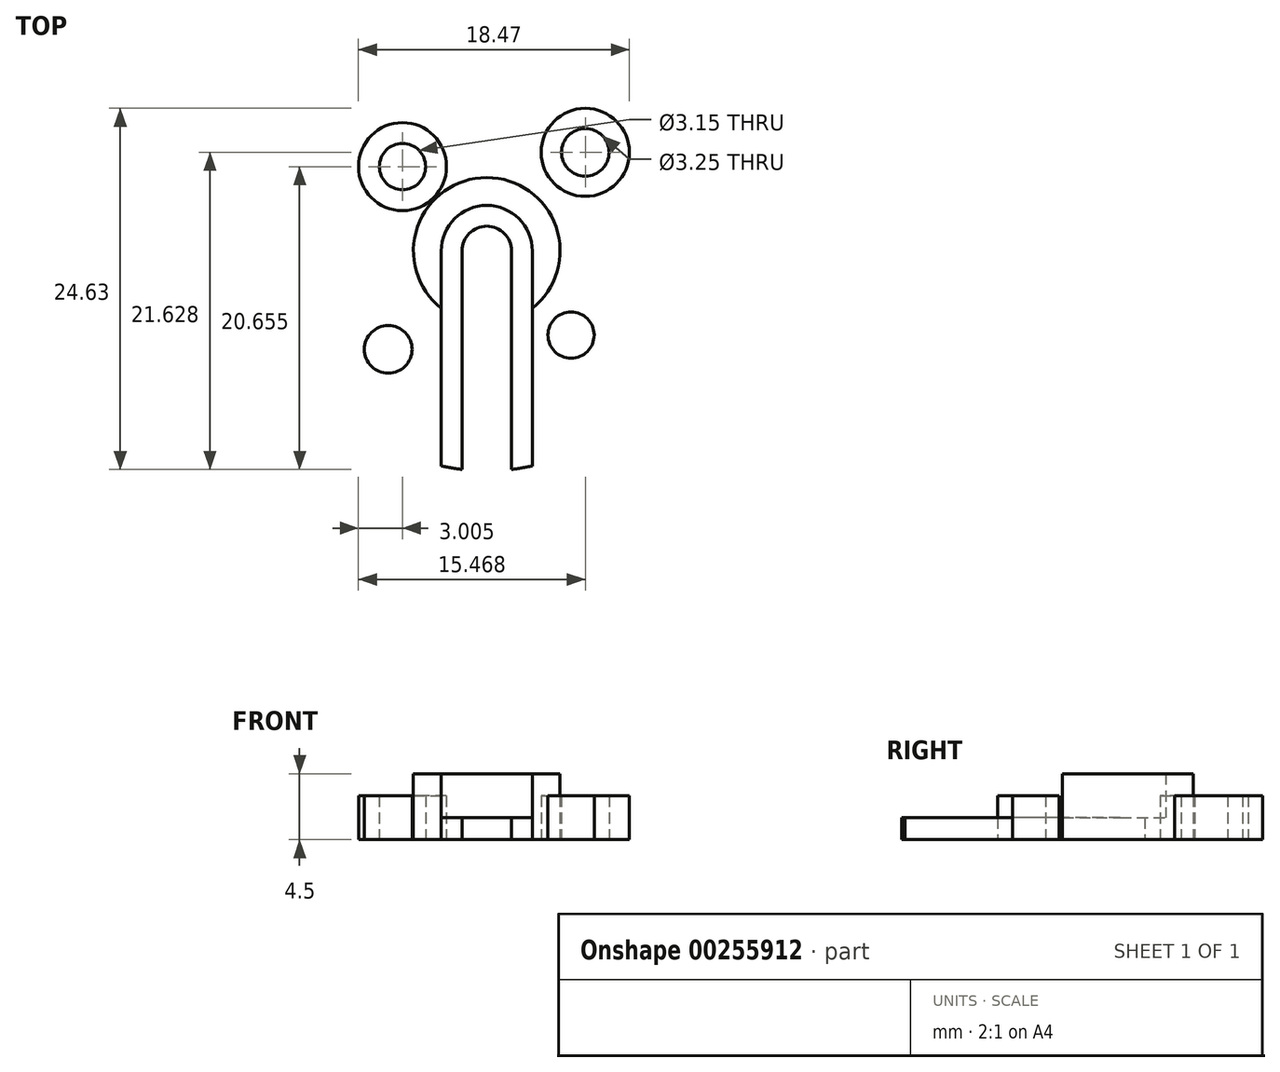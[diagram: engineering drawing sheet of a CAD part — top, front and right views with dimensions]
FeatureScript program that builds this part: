
annotation { "Feature Type Name" : "Feature", "Feature Type Description" : "" }
export const myFeature = defineFeature(function(context is Context, id is Id, definition is map)
    precondition{}
    {
        {
            var Q0;
            Q0=qCreatedBy(makeId("Top.planeOp"),FACE);
            var sketch = newSketch(context, id + "F0", { "sketchPlane" : qUnion([Q0])});
            skCircle(sketch, "E0", {"center": v(0, 0) * mm, "radius": 1.68 * mm});
            skCircle(sketch, "E1", {"center": v(0, 0) * mm, "radius": 3.1 * mm});
            skCircle(sketch, "E2", {"center": v(0, 0) * mm, "radius": 5 * mm});
            skLineSegment(sketch, "E3", {"start": v(-1.68, 0) * mm, "end": v(-1.68, -14.9) * mm});
            skLineSegment(sketch, "E4", {"start": v(-3.1, 0) * mm, "end": v(-3.1, -14.68) * mm});
            skLineSegment(sketch, "E5.MirrorCS", {"start": v(1.68, 0) * mm, "end": v(1.68, -14.9) * mm});
            skLineSegment(sketch, "E6.MirrorCS", {"start": v(3.1, 0) * mm, "end": v(3.1, -14.68) * mm});
            skCircle(sketch, "E7", {"center": v(0, 0) * mm, "radius": 9.5 * mm, "construction": true});
            skCircle(sketch, "E8", {"center": v(0, 0) * mm, "radius": 8.12 * mm, "construction": true});
            skCircle(sketch, "E9", {"center": v(-5.75, 5.75) * mm, "radius": 1.57 * mm});
            skCircle(sketch, "E10", {"center": v(6.72, 6.72) * mm, "radius": 1.63 * mm});
            skLineSegment(sketch, "E11", {"start": v(0, 0) * mm, "end": v(-5.75, 5.75) * mm, "construction": true});
            skLineSegment(sketch, "E12", {"start": v(0, 0) * mm, "end": v(6.72, 6.72) * mm, "construction": true});
            skCircle(sketch, "E13.MirrorC", {"center": v(5.75, -5.75) * mm, "radius": 1.57 * mm});
            skCircle(sketch, "E14.MirrorC", {"center": v(-6.72, -6.72) * mm, "radius": 1.63 * mm});
            skCircle(sketch, "E15", {"center": v(0, 0) * mm, "radius": 15 * mm});
            skCircle(sketch, "E16", {"center": v(-12.42, 0) * mm, "radius": 1.57 * mm});
            skCircle(sketch, "E17.MirrorC", {"center": v(12.42, 0) * mm, "radius": 1.57 * mm});
            skCircle(sketch, "E18.MirrorC", {"center": v(0, 12.42) * mm, "radius": 1.57 * mm});
            skCircle(sketch, "E19", {"center": v(-6.72, -6.72) * mm, "radius": 3 * mm});
            skCircle(sketch, "E20", {"center": v(5.75, -5.75) * mm, "radius": 3 * mm});
            skCircle(sketch, "E21.MirrorC", {"center": v(6.72, 6.72) * mm, "radius": 3 * mm});
            skCircle(sketch, "E22.MirrorC", {"center": v(-5.75, 5.75) * mm, "radius": 3 * mm});
            skSolve(sketch);
        }
        {
            var Q0;
            {var subQ0=sQuery(id+"F0.wireOp",EDGE,"E4");Q0=makeQuery(id+"F0.imprint","IMPRINT",FACE,{"disambiguationData":[TD([[makeQuery(id+"F0.imprint","IMPRINT",EDGE,{"derivedFrom":subQ0}),1.0]])]});}
            var Q1;
            {var subQ0=sQuery(id+"F0.wireOp",EDGE,"E6.MirrorCS");Q1=makeQuery(id+"F0.imprint","IMPRINT",FACE,{"disambiguationData":[TD([[makeQuery(id+"F0.imprint","IMPRINT",EDGE,{"derivedFrom":subQ0}),-1.0]])]});}
            var Q2;
            {var subQ2=sQuery(id+"F0.wireOp",EDGE,"E3");var subQ6=sQuery(id+"F0.wireOp",EDGE,"E0");var subQ9=makeQuery(id+"F0.imprint","INTERSECT",VERTEX,{"derivedFrom":[subQ6,subQ2]});Q2=makeQuery(id+"F0.imprint","IMPRINT",FACE,{"disambiguationData":[TD([[makeQuery(id+"F0.imprint","IMPRINT",EDGE,{"disambiguationData":[TD([[subQ9,1.0]])],"derivedFrom":subQ6}),-1.0]])]});}
            var Q3;
            {var subQ0=sQuery(id+"F0.wireOp",EDGE,"E19");var subQ1=sQuery(id+"F0.wireOp",EDGE,"E4");var subQ2=makeQuery(id+"F0.imprint","INTERSECT",VERTEX,{"disambiguationData":[OD(0.0)],"derivedFrom":[subQ1,subQ0]});Q3=makeQuery(id+"F0.imprint","IMPRINT",FACE,{"disambiguationData":[TD([[makeQuery(id+"F0.imprint","IMPRINT",EDGE,{"disambiguationData":[TD([[subQ2,-1.0]])],"derivedFrom":subQ1}),1.0]])]});}
            var Q4;
            {var subQ0=sQuery(id+"F0.wireOp",EDGE,"E4");var subQ1=sQuery(id+"F0.wireOp",EDGE,"E1");var subQ2=makeQuery(id+"F0.imprint","INTERSECT",VERTEX,{"derivedFrom":[subQ1,subQ0]});Q4=makeQuery(id+"F0.imprint","IMPRINT",FACE,{"disambiguationData":[TD([[makeQuery(id+"F0.imprint","IMPRINT",EDGE,{"disambiguationData":[TD([[subQ2,-1.0]])],"derivedFrom":subQ1}),-1.0]])]});}
            var Q5;
            {var subQ0=sQuery(id+"F0.wireOp",EDGE,"E4");var subQ1=sQuery(id+"F0.wireOp",EDGE,"E1");var subQ2=makeQuery(id+"F0.imprint","INTERSECT",VERTEX,{"derivedFrom":[subQ1,subQ0]});Q5=makeQuery(id+"F0.imprint","IMPRINT",FACE,{"disambiguationData":[TD([[makeQuery(id+"F0.imprint","IMPRINT",EDGE,{"disambiguationData":[TD([[subQ2,1.0]])],"derivedFrom":subQ1}),-1.0]])]});}
            var Q6;
            {var subQ0=sQuery(id+"F0.wireOp",EDGE,"E6.MirrorCS");var subQ1=sQuery(id+"F0.wireOp",EDGE,"E1");var subQ2=makeQuery(id+"F0.imprint","INTERSECT",VERTEX,{"derivedFrom":[subQ1,subQ0]});Q6=makeQuery(id+"F0.imprint","IMPRINT",FACE,{"disambiguationData":[TD([[makeQuery(id+"F0.imprint","IMPRINT",EDGE,{"disambiguationData":[TD([[subQ2,1.0]])],"derivedFrom":subQ1}),-1.0]])]});}
            var Q7;
            {var subQ0=sQuery(id+"F0.wireOp",EDGE,"E20");var subQ1=sQuery(id+"F0.wireOp",EDGE,"E6.MirrorCS");var subQ2=makeQuery(id+"F0.imprint","INTERSECT",VERTEX,{"disambiguationData":[OD(0.0)],"derivedFrom":[subQ1,subQ0]});Q7=makeQuery(id+"F0.imprint","IMPRINT",FACE,{"disambiguationData":[TD([[makeQuery(id+"F0.imprint","IMPRINT",EDGE,{"disambiguationData":[TD([[subQ2,-1.0]])],"derivedFrom":subQ1}),-1.0]])]});}
            extrude(context, id + "F1", {"entities" : qUnion([Q0, Q1, Q2, Q3, Q4, Q5, Q6, Q7]), "depth" : 1.5 * mm});
        }
        {
            var Q0;
            {var subQ0=sQuery(id+"F0.wireOp",EDGE,"E4");Q0=makeQuery(id+"F0.imprint","IMPRINT",FACE,{"disambiguationData":[TD([[makeQuery(id+"F0.imprint","IMPRINT",EDGE,{"derivedFrom":subQ0}),-1.0]])]});}
            var Q1;
            Q1=makeQuery(id+"F0.imprint","IMPRINT",FACE,{"disambiguationData":[TD([[makeQuery(id+"F0.imprint","IMPRINT",EDGE,{"derivedFrom":sQuery(id+"F0.wireOp",EDGE,"E16")}),-1.0]])]});
            extrude(context, id + "F2", {"entities" : qUnion([Q0, Q1]), "operationType" : NewBodyOperationType.ADD, "depth" : 4.5 * mm});
        }
        {
            var Q0;
            Q0=makeQuery(id+"F0.imprint","IMPRINT",FACE,{"disambiguationData":[TD([[makeQuery(id+"F0.imprint","IMPRINT",EDGE,{"derivedFrom":sQuery(id+"F0.wireOp",EDGE,"E9")}),-1.0]])]});
            var Q1;
            Q1=makeQuery(id+"F0.imprint","IMPRINT",FACE,{"disambiguationData":[TD([[makeQuery(id+"F0.imprint","IMPRINT",EDGE,{"derivedFrom":sQuery(id+"F0.wireOp",EDGE,"E10")}),-1.0]])]});
            var Q2;
            Q2=makeQuery(id+"F0.imprint","IMPRINT",FACE,{"disambiguationData":[TD([[makeQuery(id+"F0.imprint","IMPRINT",EDGE,{"derivedFrom":sQuery(id+"F0.wireOp",EDGE,"E13.MirrorC")}),1.0]])]});
            var Q3;
            Q3=makeQuery(id+"F0.imprint","IMPRINT",FACE,{"disambiguationData":[TD([[makeQuery(id+"F0.imprint","IMPRINT",EDGE,{"derivedFrom":sQuery(id+"F0.wireOp",EDGE,"E14.MirrorC")}),1.0]])]});
            extrude(context, id + "F3", {"entities" : qUnion([Q0, Q1, Q2, Q3]), "operationType" : NewBodyOperationType.ADD, "depth" : 3 * mm});
        }
    });
